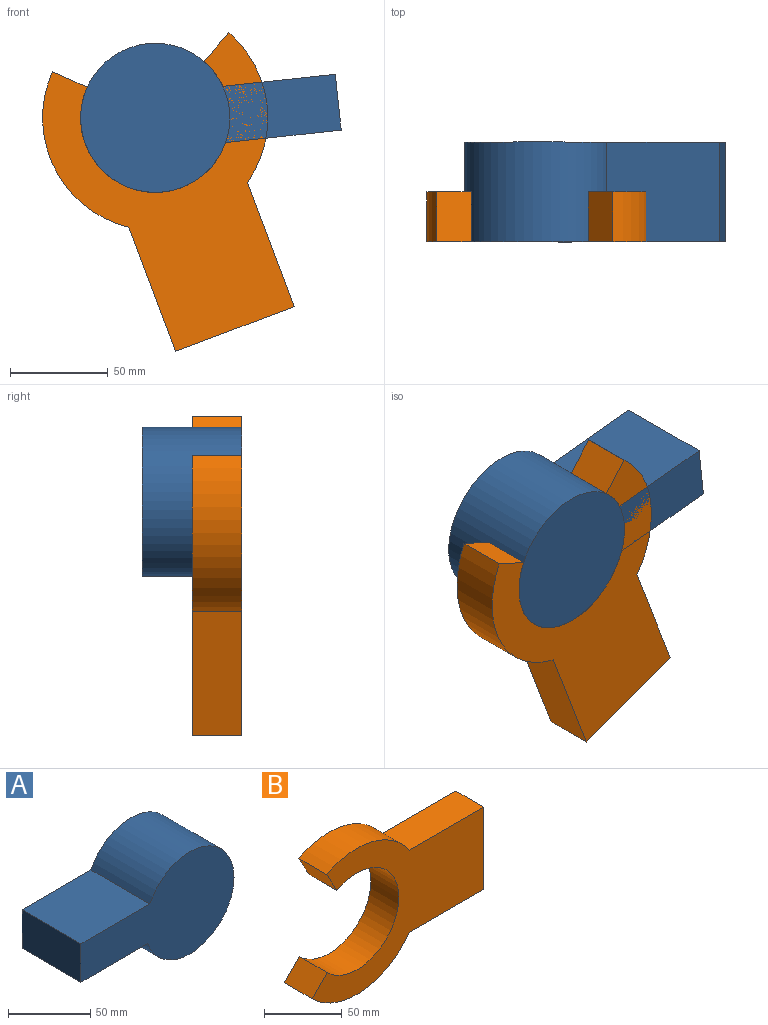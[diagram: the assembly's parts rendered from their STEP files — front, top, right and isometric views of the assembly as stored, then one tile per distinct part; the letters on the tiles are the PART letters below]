
ASSEMBLY  parts=2 mates=1
PART A: 6 faces, bbox 131.9x50.8x76.2 mm
  f0: plane 59.39x50.8mm, normal (0,0,1), area 3016.9mm2, adj f1,f3,f4,f5
  f1: plane 50.8x28.69mm, normal (-1,0,0), area 1457.5mm2, adj f0,f2,f4,f5
  f2: plane 57.72x50.8mm, normal (0,0,-1), area 2932.3mm2, adj f1,f3,f4,f5
  f3: cylinder r=38.1mm len=76.2mm, axis (0,1,0), area 10664mm2, adj f0,f2,f4,f5
  f4: plane 131.88x76.2mm, normal (0,-1,0), area 6186.1mm2, adj f0,f1,f2,f3
  f5: plane 131.88x76.2mm, normal (0,1,0), area 6186.1mm2, adj f0,f1,f2,f3
PART B: 10 faces, bbox 155.8x25.4x115 mm
  f0: cylinder r=38.1mm len=76.2mm, axis (0,1,0), area 4279.7mm2, adj f1,f7,f8,f9
  f1: plane 25.4x13.74mm, normal (-0.71,0,0.71), area 492.9mm2, adj f0,f2,f8,f9
  f2: cylinder r=57.5mm len=88.14mm, axis (0,1,0), area 2566.3mm2, adj f1,f3,f8,f9
  f3: plane 67.71x25.4mm, normal (0,0,-1), area 1719.9mm2, adj f2,f4,f8,f9
  f4: plane 64.7x25.4mm, normal (1,0,0), area 1643.5mm2, adj f3,f5,f8,f9
  f5: plane 67.71x25.4mm, normal (0,0,1), area 1719.7mm2, adj f4,f6,f8,f9
  f6: cylinder r=57.5mm len=74.96mm, axis (0,1,0), area 2147.6mm2, adj f5,f7,f8,f9
  f7: plane 25.4x17.06mm, normal (-0.88,0,-0.48), area 492.9mm2, adj f0,f6,f8,f9
  f8: plane 155.85x115.01mm, normal (0,-1,0), area 8045.3mm2, adj f0,f1,f2,f3,f4,f5,f6,f7
  f9: plane 155.85x115.01mm, normal (0,1,0), area 8045.3mm2, adj f0,f1,f2,f3,f4,f5,f6,f7
PLACE A rot(axis=(0,1,0),173.9deg) t=(7.84,45.14,51.42)mm
PLACE B rot(axis=(0,1,0),69.3deg) t=(-47.28,19.74,45.5)mm
MATE revolute B.f0 <-> A.f3  axis (0,-1,0) through (-47.28,-5.66,45.5)mm
